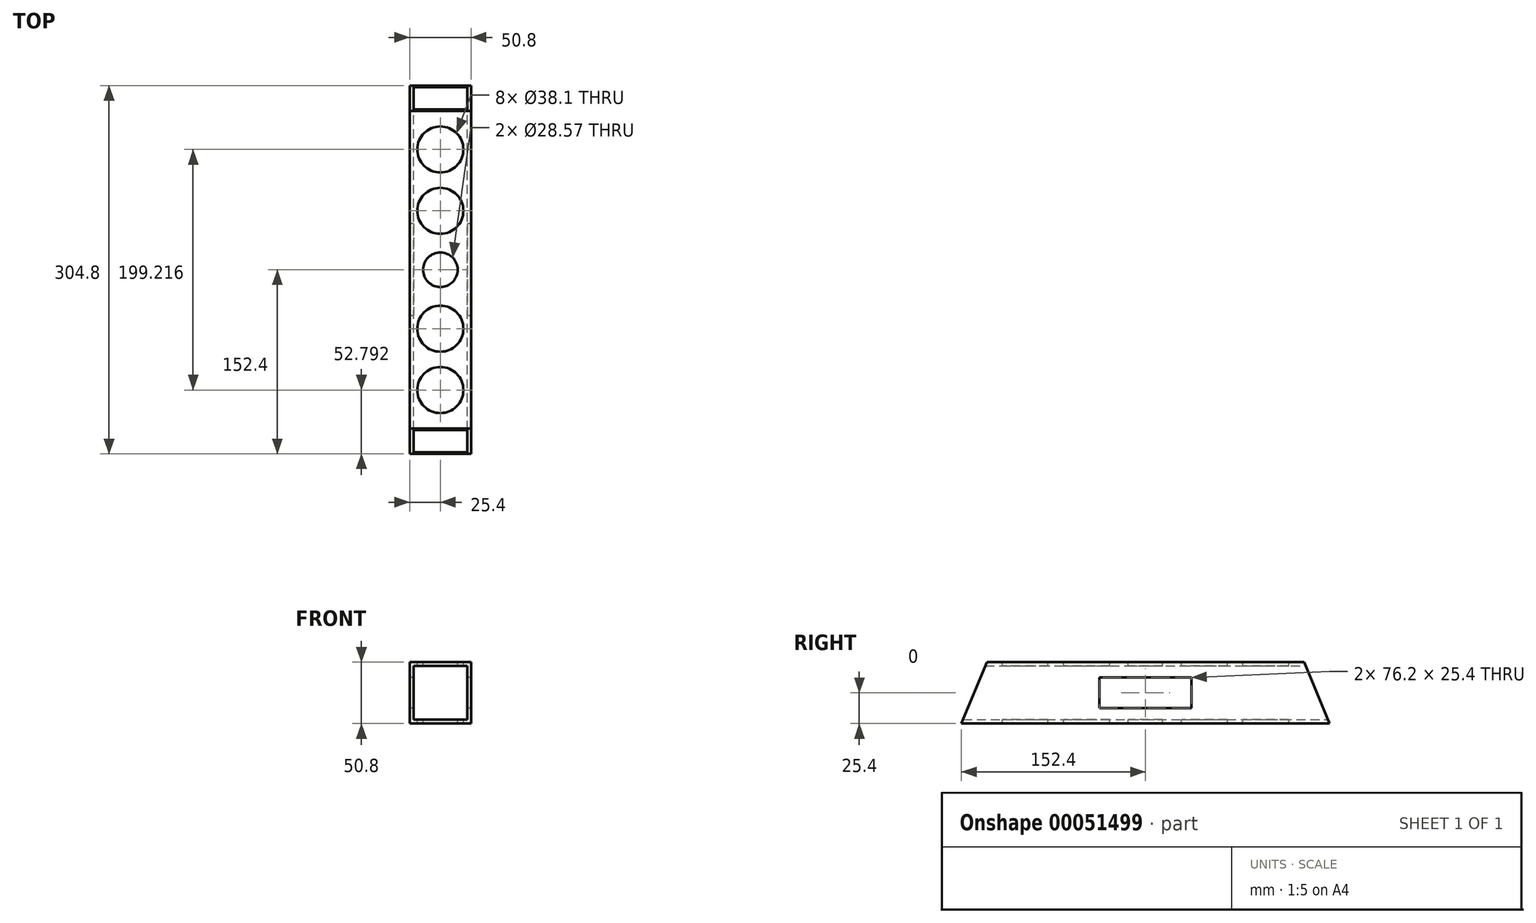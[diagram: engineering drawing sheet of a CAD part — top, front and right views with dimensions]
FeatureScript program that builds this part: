
annotation { "Feature Type Name" : "Feature", "Feature Type Description" : "" }
export const myFeature = defineFeature(function(context is Context, id is Id, definition is map)
    precondition{}
    {
        {
            var Q0;
            Q0=qCreatedBy(makeId("Front.planeOp"),FACE);
            var sketch = newSketch(context, id + "F0", { "sketchPlane" : qUnion([Q0])});
            skLineSegment(sketch, "E0.rect.bottom", {"start": v(25.4, 25.4) * mm, "end": v(-25.4, 25.4) * mm});
            skLineSegment(sketch, "E0.rect.top", {"start": v(25.4, -25.4) * mm, "end": v(-25.4, -25.4) * mm});
            skLineSegment(sketch, "E0.rect.left", {"start": v(25.4, 25.4) * mm, "end": v(25.4, -25.4) * mm});
            skLineSegment(sketch, "E0.rect.right", {"start": v(-25.4, 25.4) * mm, "end": v(-25.4, -25.4) * mm});
            skPoint(sketch, "E0.rect.middle", {"position": v(0, 0) * mm});
            skSolve(sketch);
        }
        {
            var Q0;
            Q0=makeQuery(id+"F0.imprint","IMPRINT",FACE,{"disambiguationData":[TD([[makeQuery(id+"F0.imprint","IMPRINT",EDGE,{"derivedFrom":sQuery(id+"F0.wireOp",EDGE,"E0.rect.bottom")}),1.0]])]});
            var sketch = newSketch(context, id + "F1", { "sketchPlane" : qUnion([Q0])});
            skLineSegment(sketch, "E1.rect.bottom", {"start": v(-22.23, 22.22) * mm, "end": v(22.23, 22.22) * mm});
            skLineSegment(sketch, "E1.rect.top", {"start": v(-22.23, -22.22) * mm, "end": v(22.23, -22.22) * mm});
            skLineSegment(sketch, "E1.rect.left", {"start": v(-22.23, 22.22) * mm, "end": v(-22.23, -22.22) * mm});
            skLineSegment(sketch, "E1.rect.right", {"start": v(22.23, 22.22) * mm, "end": v(22.23, -22.22) * mm});
            skPoint(sketch, "E1.rect.middle", {"position": v(0, 0) * mm});
            skSolve(sketch);
        }
        {
            var Q0;
            Q0=makeQuery(id+"F1.imprint","IMPRINT",FACE,{"disambiguationData":[TD([[makeQuery(id+"F1.imprint","IMPRINT",EDGE,{"derivedFrom":sQuery(id+"F1.wireOp",EDGE,"E1.rect.bottom")}),1.0]])]});
            extrude(context, id + "F2", {"entities" : qUnion([Q0]), "depth" : 304.8 * mm});
        }
        {
            var Q0;
            Q0=makeQuery(id+"F2.opExtrude","SWEPT_FACE",FACE,{"disambiguationData":[OSD([sQuery(id+"F0.wireOp",EDGE,"E0.rect.left")])]});
            var sketch = newSketch(context, id + "F3", { "sketchPlane" : qUnion([Q0])});
            skPoint(sketch, "E2.0.midPoint", {"position": v(-304.8, 25.4) * mm});
            skLineSegment(sketch, "E3", {"start": v(-304.8, 25.4) * mm, "end": v(-304.8, -25.4) * mm});
            skLineSegment(sketch, "E4", {"start": v(-304.8, -25.4) * mm, "end": v(-283.76, 25.4) * mm});
            skLineSegment(sketch, "E5", {"start": v(-283.76, 25.4) * mm, "end": v(-304.8, 25.4) * mm});
            skSolve(sketch);
        }
        {
            var Q0;
            Q0=makeQuery(id+"F3.imprint","IMPRINT",FACE,{"disambiguationData":[TD([[makeQuery(id+"F3.imprint","IMPRINT",EDGE,{"derivedFrom":sQuery(id+"F3.wireOp",EDGE,"E3")}),1.0]])]});
            extrude(context, id + "F4", {"entities" : qUnion([Q0]), "operationType" : NewBodyOperationType.REMOVE, "endBound" : BoundingType.THROUGH_ALL, "oppositeDirection" : true, "depth" : 25.4 * mm});
        }
        {
            var Q0;
            Q0=makeQuery(id+"F2.opExtrude","SWEPT_FACE",FACE,{"disambiguationData":[OSD([sQuery(id+"F0.wireOp",EDGE,"E0.rect.left")])]});
            var sketch = newSketch(context, id + "F5", { "sketchPlane" : qUnion([Q0])});
            skLineSegment(sketch, "E6", {"start": v(0, 25.4) * mm, "end": v(-21.04, 25.4) * mm});
            skLineSegment(sketch, "E7", {"start": v(-21.04, 25.4) * mm, "end": v(0, -25.4) * mm});
            skLineSegment(sketch, "E8", {"start": v(0, -25.4) * mm, "end": v(0, 25.4) * mm});
            skSolve(sketch);
        }
        {
            var Q0;
            Q0=makeQuery(id+"F5.imprint","IMPRINT",FACE,{"disambiguationData":[TD([[makeQuery(id+"F5.imprint","IMPRINT",EDGE,{"derivedFrom":sQuery(id+"F5.wireOp",EDGE,"E6")}),-1.0]])]});
            extrude(context, id + "F6", {"entities" : qUnion([Q0]), "operationType" : NewBodyOperationType.REMOVE, "oppositeDirection" : true, "depth" : 127 * mm});
        }
        {
            var Q0;
            Q0=makeQuery(id+"F2.opExtrude","SWEPT_FACE",FACE,{"disambiguationData":[OSD([sQuery(id+"F0.wireOp",EDGE,"E0.rect.bottom")])]});
            var sketch = newSketch(context, id + "F7", { "sketchPlane" : qUnion([Q0])});
            skCircle(sketch, "E9", {"center": v(0, -152.4) * mm, "radius": 14.29 * mm});
            skPoint(sketch, "E9.centerSnap0", {"position": v(-25.4, -152.4) * mm});
            skSolve(sketch);
        }
        {
            var Q0;
            Q0=makeQuery(id+"F7.imprint","IMPRINT",FACE,{"disambiguationData":[TD([[makeQuery(id+"F7.imprint","IMPRINT",EDGE,{"derivedFrom":sQuery(id+"F7.wireOp",EDGE,"E9")}),1.0]])]});
            extrude(context, id + "F8", {"entities" : qUnion([Q0]), "operationType" : NewBodyOperationType.REMOVE, "endBound" : BoundingType.THROUGH_ALL, "oppositeDirection" : true, "depth" : 25.4 * mm});
        }
        {
            var Q0;
            Q0=makeQuery(id+"F2.opExtrude","SWEPT_FACE",FACE,{"disambiguationData":[OSD([sQuery(id+"F0.wireOp",EDGE,"E0.rect.right")])]});
            var sketch = newSketch(context, id + "F9", { "sketchPlane" : qUnion([Q0])});
            skLineSegment(sketch, "E10.rect.bottom", {"start": v(190.5, -12.7) * mm, "end": v(114.3, -12.7) * mm});
            skLineSegment(sketch, "E10.rect.top", {"start": v(190.5, 12.7) * mm, "end": v(114.3, 12.7) * mm});
            skLineSegment(sketch, "E10.rect.left", {"start": v(190.5, -12.7) * mm, "end": v(190.5, 12.7) * mm});
            skLineSegment(sketch, "E10.rect.right", {"start": v(114.3, -12.7) * mm, "end": v(114.3, 12.7) * mm});
            skPoint(sketch, "E10.rect.middle", {"position": v(152.4, 0) * mm});
            skPoint(sketch, "E10.rect.middle.positionSnap0", {"position": v(152.4, -25.4) * mm});
            skPoint(sketch, "E10.rect.centerSnap0", {"position": v(152.4, -25.4) * mm});
            skSolve(sketch);
        }
        {
            var Q0;
            Q0=makeQuery(id+"F9.imprint","IMPRINT",FACE,{"disambiguationData":[TD([[makeQuery(id+"F9.imprint","IMPRINT",EDGE,{"derivedFrom":sQuery(id+"F9.wireOp",EDGE,"E10.rect.bottom")}),-1.0]])]});
            extrude(context, id + "F10", {"entities" : qUnion([Q0]), "operationType" : NewBodyOperationType.REMOVE, "endBound" : BoundingType.THROUGH_ALL, "oppositeDirection" : true, "depth" : 25.4 * mm});
        }
        {
            var Q0;
            Q0=makeQuery(id+"F2.opExtrude","SWEPT_FACE",FACE,{"disambiguationData":[OSD([sQuery(id+"F0.wireOp",EDGE,"E0.rect.bottom")])]});
            var sketch = newSketch(context, id + "F11", { "sketchPlane" : qUnion([Q0])});
            skCircle(sketch, "E11", {"center": v(0, -252) * mm, "radius": 19.05 * mm});
            skCircle(sketch, "E12.1.0.0", {"center": v(0, -201.2) * mm, "radius": 19.05 * mm});
            skLineSegment(sketch, "E12.direction1", {"start": v(0, -252) * mm, "end": v(0, -201.2) * mm, "construction": true});
            skCircle(sketch, "E13", {"center": v(0, -103.6) * mm, "radius": 19.05 * mm});
            skCircle(sketch, "E14.1.0.0", {"center": v(0, -52.8) * mm, "radius": 19.05 * mm});
            skLineSegment(sketch, "E14.direction1", {"start": v(0, -103.6) * mm, "end": v(0, -52.8) * mm, "construction": true});
            skSolve(sketch);
        }
        {
            var Q0;
            Q0=makeQuery(id+"F11.imprint","IMPRINT",FACE,{"disambiguationData":[TD([[makeQuery(id+"F11.imprint","IMPRINT",EDGE,{"derivedFrom":sQuery(id+"F11.wireOp",EDGE,"E11")}),1.0]])]});
            var Q1;
            Q1=makeQuery(id+"F11.imprint","IMPRINT",FACE,{"disambiguationData":[TD([[makeQuery(id+"F11.imprint","IMPRINT",EDGE,{"derivedFrom":sQuery(id+"F11.wireOp",EDGE,"E12.1.0.0")}),1.0]])]});
            var Q2;
            Q2=makeQuery(id+"F11.imprint","IMPRINT",FACE,{"disambiguationData":[TD([[makeQuery(id+"F11.imprint","IMPRINT",EDGE,{"derivedFrom":sQuery(id+"F11.wireOp",EDGE,"E13")}),1.0]])]});
            var Q3;
            Q3=makeQuery(id+"F11.imprint","IMPRINT",FACE,{"disambiguationData":[TD([[makeQuery(id+"F11.imprint","IMPRINT",EDGE,{"derivedFrom":sQuery(id+"F11.wireOp",EDGE,"E14.1.0.0")}),1.0]])]});
            extrude(context, id + "F12", {"entities" : qUnion([Q0, Q1, Q2, Q3]), "operationType" : NewBodyOperationType.REMOVE, "oppositeDirection" : true, "depth" : 50.8 * mm});
        }
    });
